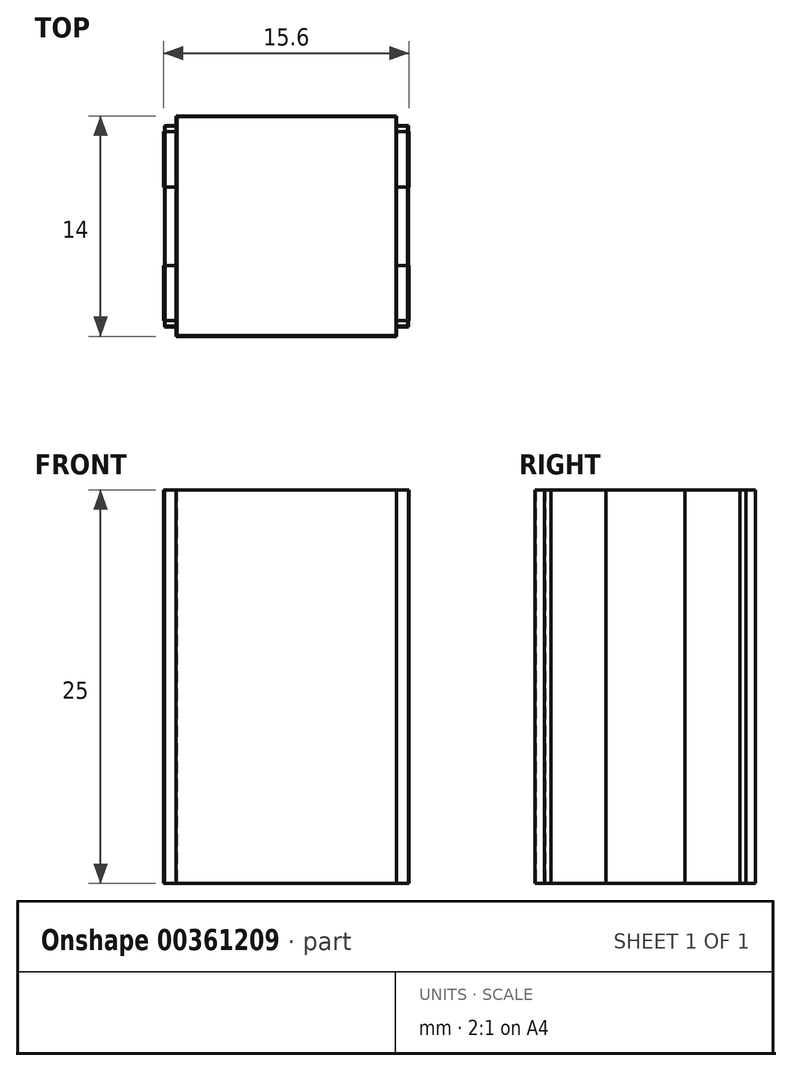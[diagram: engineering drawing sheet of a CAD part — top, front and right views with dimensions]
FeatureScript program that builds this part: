
annotation { "Feature Type Name" : "Feature", "Feature Type Description" : "" }
export const myFeature = defineFeature(function(context is Context, id is Id, definition is map)
    precondition{}
    {
        {
            var Q0;
            Q0=qCreatedBy(makeId("Top.planeOp"),FACE);
            var sketch = newSketch(context, id + "F0", { "sketchPlane" : qUnion([Q0])});
            skLineSegment(sketch, "E0.bottom", {"start": v(7, 7) * mm, "end": v(-7, 7) * mm});
            skLineSegment(sketch, "E0.top", {"start": v(7, -7) * mm, "end": v(-7, -7) * mm});
            skLineSegment(sketch, "E0.left", {"start": v(7, 7) * mm, "end": v(7, -7) * mm});
            skLineSegment(sketch, "E0.right", {"start": v(-7, 7) * mm, "end": v(-7, -7) * mm});
            skPoint(sketch, "E0.middle", {"position": v(0, 0) * mm});
            skSolve(sketch);
        }
        {
            var Q0;
            Q0 = qSketchRegion(id + "F0", true);
            extrude(context, id + "F1", {"entities" : qUnion([Q0]), "depth" : 25 * mm, "offsetDistance" : 25 * mm, "symmetric" : true});
        }
        {
            var Q0;
            Q0=qCreatedBy(makeId("Top.planeOp"),FACE);
            var sketch = newSketch(context, id + "F2", { "sketchPlane" : qUnion([Q0])});
            skLineSegment(sketch, "E1.bottom", {"start": v(7, 7) * mm, "end": v(-7, 7) * mm});
            skLineSegment(sketch, "E1.top", {"start": v(7, -7) * mm, "end": v(-7, -7) * mm});
            skLineSegment(sketch, "E1.left", {"start": v(7, 7) * mm, "end": v(7, -7) * mm});
            skLineSegment(sketch, "E1.right", {"start": v(-7, 7) * mm, "end": v(-7, -7) * mm});
            skPoint(sketch, "E1.middle", {"position": v(0, 0) * mm});
            skLineSegment(sketch, "E2.bottom", {"start": v(7.75, 6.4) * mm, "end": v(-7.75, 6.4) * mm});
            skLineSegment(sketch, "E2.top", {"start": v(7.75, -6.4) * mm, "end": v(-7.75, -6.4) * mm});
            skLineSegment(sketch, "E2.left", {"start": v(7.75, 6.4) * mm, "end": v(7.75, -6.4) * mm});
            skLineSegment(sketch, "E2.right", {"start": v(-7.75, 6.4) * mm, "end": v(-7.75, -6.4) * mm});
            skSolve(sketch);
        }
        {
            var Q0;
            Q0 = qSketchRegion(id + "F2", true);
            extrude(context, id + "F3", {"entities" : qUnion([Q0]), "depth" : 25 * mm, "offsetDistance" : 25 * mm, "symmetric" : true});
        }
        {
            var Q0;
            Q0=qCreatedBy(makeId("Top.planeOp"),FACE);
            var sketch = newSketch(context, id + "F4", { "sketchPlane" : qUnion([Q0])});
            skLineSegment(sketch, "E3.bottom", {"start": v(7, 7) * mm, "end": v(-7, 7) * mm});
            skLineSegment(sketch, "E3.top", {"start": v(7, -7) * mm, "end": v(-7, -7) * mm});
            skLineSegment(sketch, "E3.left", {"start": v(7, 7) * mm, "end": v(7, -7) * mm});
            skLineSegment(sketch, "E3.right", {"start": v(-7, 7) * mm, "end": v(-7, -7) * mm});
            skPoint(sketch, "E3.middle", {"position": v(0, 0) * mm});
            skLineSegment(sketch, "E4", {"start": v(0, 0) * mm, "end": v(2.78, 0) * mm, "construction": true});
            skLineSegment(sketch, "E5.bottom", {"start": v(7, 6) * mm, "end": v(7.8, 6) * mm});
            skLineSegment(sketch, "E5.top", {"start": v(7, 2.5) * mm, "end": v(7.8, 2.5) * mm});
            skLineSegment(sketch, "E5.left", {"start": v(7, 6) * mm, "end": v(7, 2.5) * mm});
            skLineSegment(sketch, "E5.right", {"start": v(7.8, 6) * mm, "end": v(7.8, 2.5) * mm});
            skLineSegment(sketch, "E6", {"start": v(0, 0) * mm, "end": v(0, 2.07) * mm, "construction": true});
            skLineSegment(sketch, "E7.MirrorCS", {"start": v(7, -2.5) * mm, "end": v(7.8, -2.5) * mm});
            skLineSegment(sketch, "E8.MirrorCS", {"start": v(7.8, -6) * mm, "end": v(7.8, -2.5) * mm});
            skLineSegment(sketch, "E9.MirrorCS", {"start": v(7, -6) * mm, "end": v(7.8, -6) * mm});
            skLineSegment(sketch, "E10.MirrorCS", {"start": v(-7, -6) * mm, "end": v(-7.8, -6) * mm});
            skLineSegment(sketch, "E11.MirrorCS", {"start": v(-7, 6) * mm, "end": v(-7.8, 6) * mm});
            skLineSegment(sketch, "E12.MirrorCS", {"start": v(-7, -2.5) * mm, "end": v(-7.8, -2.5) * mm});
            skLineSegment(sketch, "E13.MirrorCS", {"start": v(-7, 2.5) * mm, "end": v(-7.8, 2.5) * mm});
            skLineSegment(sketch, "E14.MirrorCS", {"start": v(-7.8, 6) * mm, "end": v(-7.8, 2.5) * mm});
            skLineSegment(sketch, "E15.MirrorCS", {"start": v(-7.8, -6) * mm, "end": v(-7.8, -2.5) * mm});
            skSolve(sketch);
        }
        {
            var Q0;
            Q0 = qSketchRegion(id + "F4", true);
            extrude(context, id + "F5", {"entities" : qUnion([Q0]), "depth" : 25 * mm, "offsetDistance" : 25 * mm, "symmetric" : true});
        }
        {
            var Q0;
            Q0=qCreatedBy(makeId("Top.planeOp"),FACE);
            var sketch = newSketch(context, id + "F6", { "sketchPlane" : qUnion([Q0])});
            skLineSegment(sketch, "E16.bottom", {"start": v(6.95, 6.95) * mm, "end": v(-6.95, 6.95) * mm});
            skLineSegment(sketch, "E16.top", {"start": v(6.95, -6.95) * mm, "end": v(-6.95, -6.95) * mm});
            skLineSegment(sketch, "E16.left", {"start": v(6.95, 6.95) * mm, "end": v(6.95, -6.95) * mm});
            skLineSegment(sketch, "E16.right", {"start": v(-6.95, 6.95) * mm, "end": v(-6.95, -6.95) * mm});
            skPoint(sketch, "E16.middle", {"position": v(0, 0) * mm});
            skSolve(sketch);
        }
        {
            var Q0;
            Q0 = qSketchRegion(id + "F6", true);
            extrude(context, id + "F7", {"entities" : qUnion([Q0]), "depth" : 25 * mm, "offsetDistance" : 25 * mm, "symmetric" : true});
        }
        {
            var Q0;
            Q0=qCreatedBy(makeId("Top.planeOp"),FACE);
            var sketch = newSketch(context, id + "F8", { "sketchPlane" : qUnion([Q0])});
            skLineSegment(sketch, "E17.bottom", {"start": v(7, 7) * mm, "end": v(-7, 7) * mm});
            skLineSegment(sketch, "E17.top", {"start": v(7, -7) * mm, "end": v(-7, -7) * mm});
            skLineSegment(sketch, "E17.left", {"start": v(7, 7) * mm, "end": v(7, -7) * mm});
            skLineSegment(sketch, "E17.right", {"start": v(-7, 7) * mm, "end": v(-7, -7) * mm});
            skPoint(sketch, "E17.middle", {"position": v(0, 0) * mm});
            skLineSegment(sketch, "E18.bottom", {"start": v(7.7, 6.35) * mm, "end": v(-7.7, 6.35) * mm});
            skLineSegment(sketch, "E18.top", {"start": v(7.7, -6.35) * mm, "end": v(-7.7, -6.35) * mm});
            skLineSegment(sketch, "E18.left", {"start": v(7.7, 6.35) * mm, "end": v(7.7, -6.35) * mm});
            skLineSegment(sketch, "E18.right", {"start": v(-7.7, 6.35) * mm, "end": v(-7.7, -6.35) * mm});
            skSolve(sketch);
        }
        {
            var Q0;
            Q0 = qSketchRegion(id + "F8", true);
            extrude(context, id + "F9", {"entities" : qUnion([Q0]), "depth" : 25 * mm, "offsetDistance" : 25 * mm, "symmetric" : true});
        }
    });
